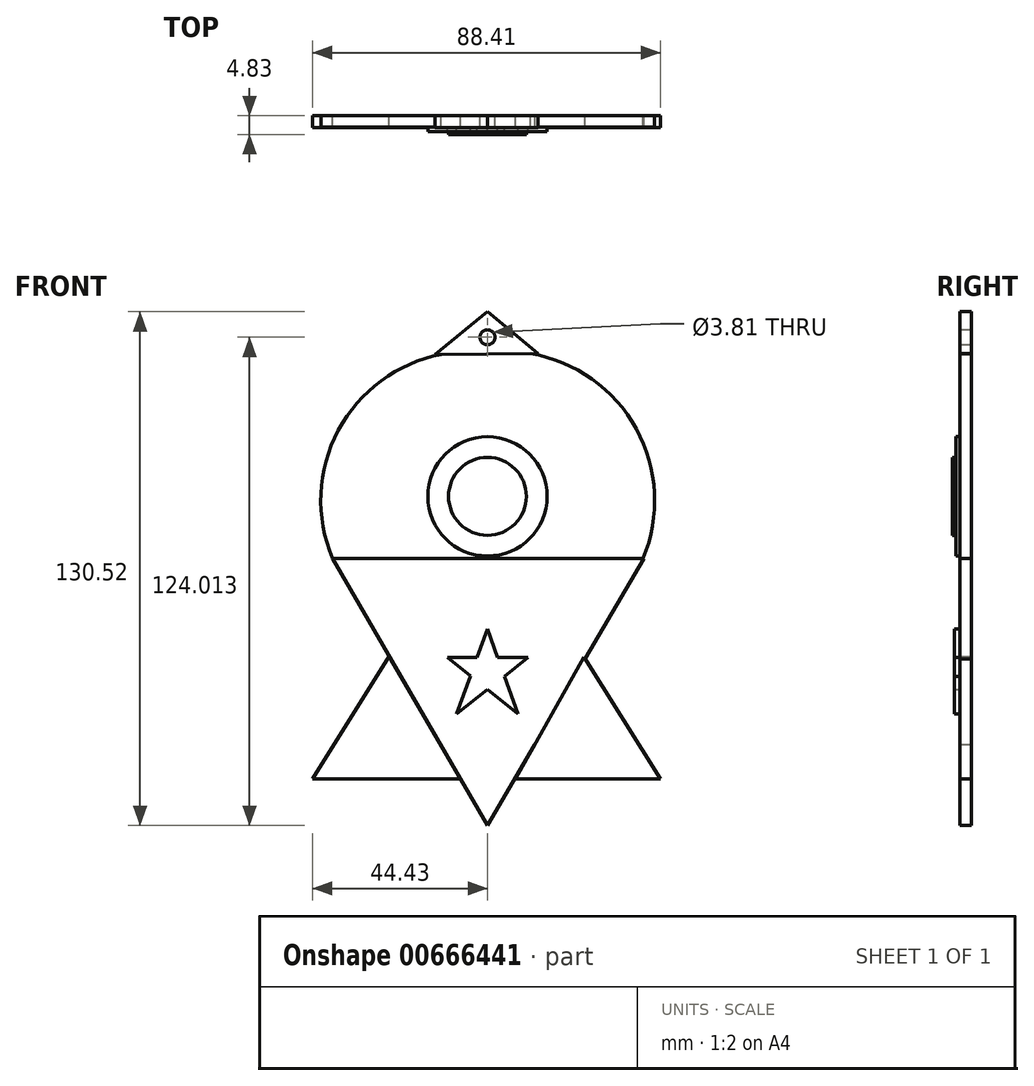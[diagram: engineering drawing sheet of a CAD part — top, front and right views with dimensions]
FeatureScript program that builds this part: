
annotation { "Feature Type Name" : "Feature", "Feature Type Description" : "" }
export const myFeature = defineFeature(function(context is Context, id is Id, definition is map)
    precondition{}
    {
        {
            var Q0;
            Q0=qCreatedBy(makeId("Front.planeOp"),FACE);
            var sketch = newSketch(context, id + "F0", { "sketchPlane" : qUnion([Q0])});
            skLineSegment(sketch, "E0", {"start": v(-39.4, 0) * mm, "end": v(0, -67.85) * mm});
            skLineSegment(sketch, "E1", {"start": v(0, -67.85) * mm, "end": v(39.76, 0) * mm});
            skLineSegment(sketch, "E2", {"start": v(-39.4, 0) * mm, "end": v(0, 0) * mm});
            skLineSegment(sketch, "E3", {"start": v(0, 0) * mm, "end": v(39.76, 0) * mm});
            skSolve(sketch);
        }
        {
            var Q0;
            Q0=qCreatedBy(makeId("Front.planeOp"),FACE);
            var sketch = newSketch(context, id + "F1", { "sketchPlane" : qUnion([Q0])});
            skArc(sketch, "E4", {"start": v(0, 52.3) * mm, "mid": v(-34.72, 37.46) * mm, "end": v(-39.4, 0) * mm});
            skArc(sketch, "E5", {"start": v(39.54, 0) * mm, "mid": v(34.82, 37.52) * mm, "end": v(0, 52.3) * mm});
            skLineSegment(sketch, "E6", {"start": v(-39.4, 0) * mm, "end": v(0, 0) * mm});
            skLineSegment(sketch, "E7", {"start": v(0, 0) * mm, "end": v(39.54, 0) * mm});
            skSolve(sketch);
        }
        {
            var Q0;
            Q0 = qSketchRegion(id + "F1", true);
            var Q1;
            Q1 = qSketchRegion(id + "F0", true);
            extrude(context, id + "F2", {"entities" : qUnion([Q0, Q1]), "depth" : 3 * mm, "offsetDistance" : 25.4 * mm});
        }
        {
            var Q0;
            Q0=qCreatedBy(makeId("Front.planeOp"),FACE);
            var sketch = newSketch(context, id + "F3", { "sketchPlane" : qUnion([Q0])});
            skLineSegment(sketch, "E8", {"start": v(-7.8, -39.57) * mm, "end": v(0, -17.96) * mm});
            skLineSegment(sketch, "E9", {"start": v(0, -17.96) * mm, "end": v(7.7, -39.57) * mm});
            skLineSegment(sketch, "E10", {"start": v(7.7, -39.57) * mm, "end": v(-10.2, -25.16) * mm});
            skLineSegment(sketch, "E11", {"start": v(-10.2, -25.16) * mm, "end": v(10.32, -25.16) * mm});
            skLineSegment(sketch, "E12", {"start": v(10.32, -25.16) * mm, "end": v(-7.8, -39.57) * mm});
            skSolve(sketch);
        }
        {
            var Q0;
            Q0 = qSketchRegion(id + "F3", true);
            extrude(context, id + "F4", {"entities" : qUnion([Q0]), "operationType" : NewBodyOperationType.ADD, "depth" : 4.32 * mm, "offsetDistance" : 25.4 * mm});
        }
        {
            var Q0;
            Q0=qCreatedBy(makeId("Front.planeOp"),FACE);
            var sketch = newSketch(context, id + "F5", { "sketchPlane" : qUnion([Q0])});
            skCircle(sketch, "E13", {"center": v(0, 15.74) * mm, "radius": 15.16 * mm});
            skSolve(sketch);
        }
        {
            var Q0;
            Q0 = qSketchRegion(id + "F5", true);
            extrude(context, id + "F6", {"entities" : qUnion([Q0]), "operationType" : NewBodyOperationType.ADD, "depth" : 4.06 * mm, "offsetDistance" : 25.4 * mm});
        }
        {
            var Q0;
            Q0=makeQuery(id+"F6.opExtrude","CAP_FACE",FACE,{"disambiguationData":[OSD([sQuery(id+"F5.wireOp",EDGE,"E13")])],"isStart":false});
            var sketch = newSketch(context, id + "F7", { "sketchPlane" : qUnion([Q0])});
            skCircle(sketch, "E14", {"center": v(0, 15.74) * mm, "radius": 9.9 * mm});
            skSolve(sketch);
        }
        {
            var Q0;
            Q0=makeQuery(id+"F7.imprint","IMPRINT",FACE,{"disambiguationData":[TD([[makeQuery(id+"F7.imprint","IMPRINT",EDGE,{"derivedFrom":sQuery(id+"F7.wireOp",EDGE,"E14")}),1.0]])]});
            extrude(context, id + "F8", {"entities" : qUnion([Q0]), "operationType" : NewBodyOperationType.ADD, "depth" : 0.76 * mm, "offsetDistance" : 25.4 * mm});
        }
        {
            var Q0;
            Q0=qCreatedBy(makeId("Front.planeOp"),FACE);
            var sketch = newSketch(context, id + "F9", { "sketchPlane" : qUnion([Q0])});
            skLineSegment(sketch, "E15", {"start": v(-13.34, 51.83) * mm, "end": v(0, 62.67) * mm});
            skLineSegment(sketch, "E16", {"start": v(0, 62.67) * mm, "end": v(12.88, 52.05) * mm});
            skLineSegment(sketch, "E17", {"start": v(12.88, 52.05) * mm, "end": v(-13.34, 51.83) * mm});
            skSolve(sketch);
        }
        {
            var Q0;
            Q0=makeQuery(id+"F9.imprint","IMPRINT",FACE,{"disambiguationData":[TD([[makeQuery(id+"F9.imprint","IMPRINT",EDGE,{"derivedFrom":sQuery(id+"F9.wireOp",EDGE,"E15")}),-1.0]])]});
            extrude(context, id + "F10", {"entities" : qUnion([Q0]), "operationType" : NewBodyOperationType.ADD, "depth" : 3.05 * mm, "offsetDistance" : 25.4 * mm});
        }
        {
            var Q0;
            Q0=qCreatedBy(makeId("Front.planeOp"),FACE);
            var sketch = newSketch(context, id + "F11", { "sketchPlane" : qUnion([Q0])});
            skPoint(sketch, "E18", {"position": v(0, 56.16) * mm});
            skSolve(sketch);
        }
        {
            var Q0;
            Q0=sQuery(id+"F11.wireOp",VERTEX,"E18");
            var Q1;
            Q1=makeQuery(id+"F2.opExtrude","SWEPT_BODY",BODY,{"disambiguationData":[OSD([sQuery(id+"F1.wireOp",EDGE,"E4"),sQuery(id+"F1.wireOp",EDGE,"E5"),sQuery(id+"F1.wireOp",EDGE,"E6"),sQuery(id+"F1.wireOp",EDGE,"E7")])]});
            hole(context, id + "F12", {"style" : HoleStyle.SIMPLE, "endStyle" : HoleEndStyle.THROUGH, "oppositeDirection" : true, "holeDiameter" : 3.8 * mm, "majorDiameter" : 6.35 * mm, "isTappedThrough" : true, "tappedDepth" : 12.7 * mm, "tapClearance" : 3, "locations" : qUnion([Q0]), "scope" : qUnion([Q1])});
        }
        {
            var Q0;
            Q0=qCreatedBy(makeId("Front.planeOp"),FACE);
            var sketch = newSketch(context, id + "F13", { "sketchPlane" : qUnion([Q0])});
            skLineSegment(sketch, "E19", {"start": v(24.55, -25.09) * mm, "end": v(43.98, -56.08) * mm});
            skLineSegment(sketch, "E20", {"start": v(43.98, -56.08) * mm, "end": v(7.1, -56.08) * mm});
            skLineSegment(sketch, "E21", {"start": v(7.1, -56.08) * mm, "end": v(24.55, -25.09) * mm});
            skSolve(sketch);
        }
        {
            var Q0;
            Q0 = qSketchRegion(id + "F13", true);
            extrude(context, id + "F14", {"entities" : qUnion([Q0]), "operationType" : NewBodyOperationType.ADD, "depth" : 3.05 * mm, "offsetDistance" : 25.4 * mm});
        }
        {
            var Q0;
            Q0=qCreatedBy(makeId("Front.planeOp"),FACE);
            var sketch = newSketch(context, id + "F15", { "sketchPlane" : qUnion([Q0])});
            skLineSegment(sketch, "E22", {"start": v(-25, -24.87) * mm, "end": v(-44.43, -56.08) * mm});
            skLineSegment(sketch, "E23", {"start": v(-44.43, -56.08) * mm, "end": v(-6.88, -56.08) * mm});
            skLineSegment(sketch, "E24", {"start": v(-6.88, -56.08) * mm, "end": v(-25, -24.87) * mm});
            skSolve(sketch);
        }
        {
            var Q0;
            Q0 = qSketchRegion(id + "F15", true);
            extrude(context, id + "F16", {"entities" : qUnion([Q0]), "depth" : 3.05 * mm, "offsetDistance" : 25.4 * mm});
        }
    });
